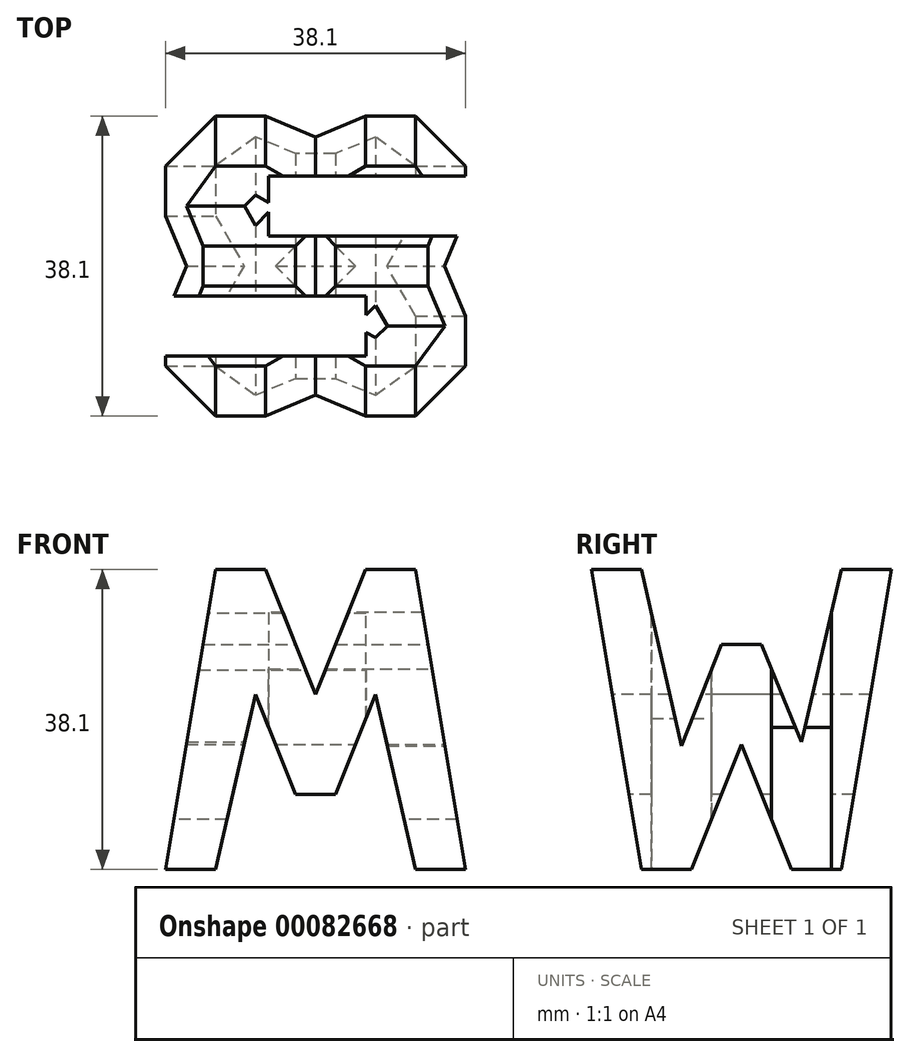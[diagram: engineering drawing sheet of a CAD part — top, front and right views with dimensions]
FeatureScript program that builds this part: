
annotation { "Feature Type Name" : "Feature", "Feature Type Description" : "" }
export const myFeature = defineFeature(function(context is Context, id is Id, definition is map)
    precondition{}
    {
        {
            var Q0;
            Q0=qCreatedBy(makeId("Front.planeOp"),FACE);
            var sketch = newSketch(context, id + "F0", { "sketchPlane" : qUnion([Q0])});
            skLineSegment(sketch, "E0", {"start": v(0, 0) * mm, "end": v(38.1, 0) * mm});
            skLineSegment(sketch, "E1", {"start": v(38.1, 0) * mm, "end": v(38.1, 38.1) * mm});
            skLineSegment(sketch, "E2", {"start": v(38.1, 38.1) * mm, "end": v(0, 38.1) * mm});
            skLineSegment(sketch, "E3", {"start": v(0, 38.1) * mm, "end": v(0, 0) * mm});
            skSolve(sketch);
        }
        {
            var Q0;
            Q0=makeQuery(id+"F0.imprint","IMPRINT",FACE,{"disambiguationData":[TD([[makeQuery(id+"F0.imprint","IMPRINT",EDGE,{"derivedFrom":sQuery(id+"F0.wireOp",EDGE,"E0")}),1.0]])]});
            extrude(context, id + "F1", {"entities" : qUnion([Q0]), "depth" : 38.1 * mm});
        }
        {
            var Q0;
            Q0=qCreatedBy(makeId("Front.planeOp"),FACE);
            cPlane(context, id + "F2", {"entities" : qUnion([Q0]), "cplaneType" : CPlaneType.OFFSET, "offset" : 38.1 * mm, "width" : 152.4 * mm, "height" : 152.4 * mm});
        }
        {
            var Q0;
            Q0=qCreatedBy(makeId("Right.planeOp"),FACE);
            cPlane(context, id + "F3", {"entities" : qUnion([Q0]), "cplaneType" : CPlaneType.OFFSET, "offset" : 38.1 * mm, "width" : 152.4 * mm, "height" : 152.4 * mm});
        }
        {
            var Q0;
            Q0=qCreatedBy(makeId("Top.planeOp"),FACE);
            cPlane(context, id + "F4", {"entities" : qUnion([Q0]), "cplaneType" : CPlaneType.OFFSET, "offset" : 38.1 * mm, "width" : 152.4 * mm, "height" : 152.4 * mm});
        }
        {
            var Q0;
            Q0=qCreatedBy(id+"F3.planeOp",FACE);
            var sketch = newSketch(context, id + "F5", { "sketchPlane" : qUnion([Q0])});
            skLineSegment(sketch, "E4", {"start": v(-38.1, 38.1) * mm, "end": v(-31.75, 0) * mm});
            skLineSegment(sketch, "E5", {"start": v(-31.75, 0) * mm, "end": v(-25.4, 0) * mm});
            skLineSegment(sketch, "E6", {"start": v(-25.4, 0) * mm, "end": v(-19.05, 15.88) * mm});
            skLineSegment(sketch, "E7", {"start": v(-19.05, 15.88) * mm, "end": v(-12.7, 0) * mm});
            skLineSegment(sketch, "E8", {"start": v(-12.7, 0) * mm, "end": v(-6.35, 0) * mm});
            skLineSegment(sketch, "E9", {"start": v(-6.35, 0) * mm, "end": v(0, 38.1) * mm});
            skLineSegment(sketch, "E10", {"start": v(0, 38.1) * mm, "end": v(-6.35, 38.1) * mm});
            skLineSegment(sketch, "E11", {"start": v(-6.35, 38.1) * mm, "end": v(-11.43, 16.18) * mm});
            skLineSegment(sketch, "E12", {"start": v(-11.43, 16.18) * mm, "end": v(-16.51, 28.58) * mm});
            skLineSegment(sketch, "E13", {"start": v(-16.51, 28.58) * mm, "end": v(-21.6, 28.58) * mm});
            skLineSegment(sketch, "E14", {"start": v(-21.6, 28.58) * mm, "end": v(-26.67, 15.67) * mm});
            skLineSegment(sketch, "E15", {"start": v(-26.67, 15.67) * mm, "end": v(-31.75, 38.1) * mm});
            skLineSegment(sketch, "E16", {"start": v(-31.75, 38.1) * mm, "end": v(-38.1, 38.1) * mm});
            skLineSegment(sketch, "E17.bottom", {"start": v(0, 0) * mm, "end": v(-38.1, 0) * mm});
            skLineSegment(sketch, "E17.top", {"start": v(0, 38.1) * mm, "end": v(-38.1, 38.1) * mm});
            skLineSegment(sketch, "E17.left", {"start": v(0, 0) * mm, "end": v(0, 38.1) * mm});
            skLineSegment(sketch, "E17.right", {"start": v(-38.1, 0) * mm, "end": v(-38.1, 38.1) * mm});
            skSolve(sketch);
        }
        {
            var Q0;
            {var subQ1=sQuery(id+"F5.wireOp",EDGE,"E11");Q0=makeQuery(id+"F5.imprint","IMPRINT",FACE,{"disambiguationData":[TD([[makeQuery(id+"F5.imprint","IMPRINT",EDGE,{"derivedFrom":subQ1}),-1.0]])]});}
            var Q1;
            {var subQ0=sQuery(id+"F5.wireOp",EDGE,"E6");Q1=makeQuery(id+"F5.imprint","IMPRINT",FACE,{"disambiguationData":[TD([[makeQuery(id+"F5.imprint","IMPRINT",EDGE,{"derivedFrom":subQ0}),-1.0]])]});}
            var Q2;
            {var subQ0=sQuery(id+"F5.wireOp",EDGE,"E4");Q2=makeQuery(id+"F5.imprint","IMPRINT",FACE,{"disambiguationData":[TD([[makeQuery(id+"F5.imprint","IMPRINT",EDGE,{"derivedFrom":subQ0}),-1.0]])]});}
            var Q3;
            {var subQ0=sQuery(id+"F5.wireOp",EDGE,"E9");Q3=makeQuery(id+"F5.imprint","IMPRINT",FACE,{"disambiguationData":[TD([[makeQuery(id+"F5.imprint","IMPRINT",EDGE,{"derivedFrom":subQ0}),-1.0]])]});}
            extrude(context, id + "F6", {"entities" : qUnion([Q0, Q1, Q2, Q3]), "operationType" : NewBodyOperationType.REMOVE, "oppositeDirection" : true, "depth" : 38.1 * mm});
        }
        {
            var Q0;
            Q0=qCreatedBy(id+"F2.planeOp",FACE);
            var sketch = newSketch(context, id + "F7", { "sketchPlane" : qUnion([Q0])});
            skLineSegment(sketch, "E18.bottom", {"start": v(0, 0) * mm, "end": v(38.1, 0) * mm});
            skLineSegment(sketch, "E18.top", {"start": v(0, 38.1) * mm, "end": v(38.1, 38.1) * mm});
            skLineSegment(sketch, "E18.left", {"start": v(0, 0) * mm, "end": v(0, 38.1) * mm});
            skLineSegment(sketch, "E18.right", {"start": v(38.1, 0) * mm, "end": v(38.1, 38.1) * mm});
            skLineSegment(sketch, "E19", {"start": v(38.1, 0) * mm, "end": v(31.75, 38.1) * mm});
            skLineSegment(sketch, "E20", {"start": v(31.75, 38.1) * mm, "end": v(25.4, 38.1) * mm});
            skLineSegment(sketch, "E21", {"start": v(25.4, 38.1) * mm, "end": v(19.05, 22.22) * mm});
            skLineSegment(sketch, "E22", {"start": v(19.05, 22.22) * mm, "end": v(12.7, 38.1) * mm});
            skLineSegment(sketch, "E23", {"start": v(12.7, 38.1) * mm, "end": v(6.35, 38.1) * mm});
            skLineSegment(sketch, "E24", {"start": v(6.35, 38.1) * mm, "end": v(0, 0) * mm});
            skLineSegment(sketch, "E25", {"start": v(6.35, 0) * mm, "end": v(11.43, 22.23) * mm});
            skLineSegment(sketch, "E26", {"start": v(11.43, 22.23) * mm, "end": v(16.51, 9.52) * mm});
            skLineSegment(sketch, "E27", {"start": v(16.51, 9.52) * mm, "end": v(21.59, 9.52) * mm});
            skLineSegment(sketch, "E28", {"start": v(21.59, 9.52) * mm, "end": v(26.67, 22.23) * mm});
            skLineSegment(sketch, "E29", {"start": v(26.67, 22.23) * mm, "end": v(31.75, 0) * mm});
            skLineSegment(sketch, "E30", {"start": v(31.75, 0) * mm, "end": v(38.1, 0) * mm});
            skSolve(sketch);
        }
        {
            var Q0;
            {var subQ0=sQuery(id+"F7.wireOp",EDGE,"E21");Q0=makeQuery(id+"F7.imprint","IMPRINT",FACE,{"disambiguationData":[TD([[makeQuery(id+"F7.imprint","IMPRINT",EDGE,{"derivedFrom":subQ0}),-1.0]])]});}
            var Q1;
            {var subQ0=sQuery(id+"F7.wireOp",EDGE,"E18.left");Q1=makeQuery(id+"F7.imprint","IMPRINT",FACE,{"disambiguationData":[TD([[makeQuery(id+"F7.imprint","IMPRINT",EDGE,{"derivedFrom":subQ0}),-1.0]])]});}
            var Q2;
            {var subQ2=sQuery(id+"F7.wireOp",EDGE,"E25");Q2=makeQuery(id+"F7.imprint","IMPRINT",FACE,{"disambiguationData":[TD([[makeQuery(id+"F7.imprint","IMPRINT",EDGE,{"derivedFrom":subQ2}),-1.0]])]});}
            var Q3;
            {var subQ0=sQuery(id+"F7.wireOp",EDGE,"E18.right");Q3=makeQuery(id+"F7.imprint","IMPRINT",FACE,{"disambiguationData":[TD([[makeQuery(id+"F7.imprint","IMPRINT",EDGE,{"derivedFrom":subQ0}),1.0]])]});}
            extrude(context, id + "F8", {"entities" : qUnion([Q0, Q1, Q2, Q3]), "operationType" : NewBodyOperationType.REMOVE, "oppositeDirection" : true, "depth" : 38.1 * mm});
        }
        {
            var Q0;
            Q0=qCreatedBy(id+"F4.planeOp",FACE);
            var sketch = newSketch(context, id + "F9", { "sketchPlane" : qUnion([Q0])});
            skLineSegment(sketch, "E31.bottom", {"start": v(0, 0) * mm, "end": v(38.1, 0) * mm});
            skLineSegment(sketch, "E31.top", {"start": v(0, -38.1) * mm, "end": v(38.1, -38.1) * mm});
            skLineSegment(sketch, "E31.left", {"start": v(0, 0) * mm, "end": v(0, -38.1) * mm});
            skLineSegment(sketch, "E31.right", {"start": v(38.1, 0) * mm, "end": v(38.1, -38.1) * mm});
            skLineSegment(sketch, "E32", {"start": v(38.1, -7.62) * mm, "end": v(13.1, -7.62) * mm});
            skLineSegment(sketch, "E33", {"start": v(13.1, -7.62) * mm, "end": v(13.1, -15.24) * mm});
            skLineSegment(sketch, "E34", {"start": v(13.1, -15.24) * mm, "end": v(38.1, -15.24) * mm});
            skLineSegment(sketch, "E35", {"start": v(38.1, -15.24) * mm, "end": v(38.1, -7.62) * mm});
            skLineSegment(sketch, "E36", {"start": v(0, -22.86) * mm, "end": v(25.45, -22.86) * mm});
            skLineSegment(sketch, "E37", {"start": v(25.45, -22.86) * mm, "end": v(25.45, -30.48) * mm});
            skLineSegment(sketch, "E38", {"start": v(25.45, -30.48) * mm, "end": v(0, -30.48) * mm});
            skLineSegment(sketch, "E39", {"start": v(0, -30.48) * mm, "end": v(0, -22.86) * mm});
            skSolve(sketch);
        }
        {
            var Q0;
            Q0=makeQuery(id+"F9.imprint","IMPRINT",FACE,{"disambiguationData":[TD([[makeQuery(id+"F9.imprint","IMPRINT",EDGE,{"derivedFrom":sQuery(id+"F9.wireOp",EDGE,"E32")}),1.0]])]});
            var Q1;
            Q1=makeQuery(id+"F9.imprint","IMPRINT",FACE,{"disambiguationData":[TD([[makeQuery(id+"F9.imprint","IMPRINT",EDGE,{"derivedFrom":sQuery(id+"F9.wireOp",EDGE,"E36")}),-1.0]])]});
            extrude(context, id + "F10", {"entities" : qUnion([Q0, Q1]), "operationType" : NewBodyOperationType.REMOVE, "oppositeDirection" : true, "depth" : 38.1 * mm});
        }
    });
